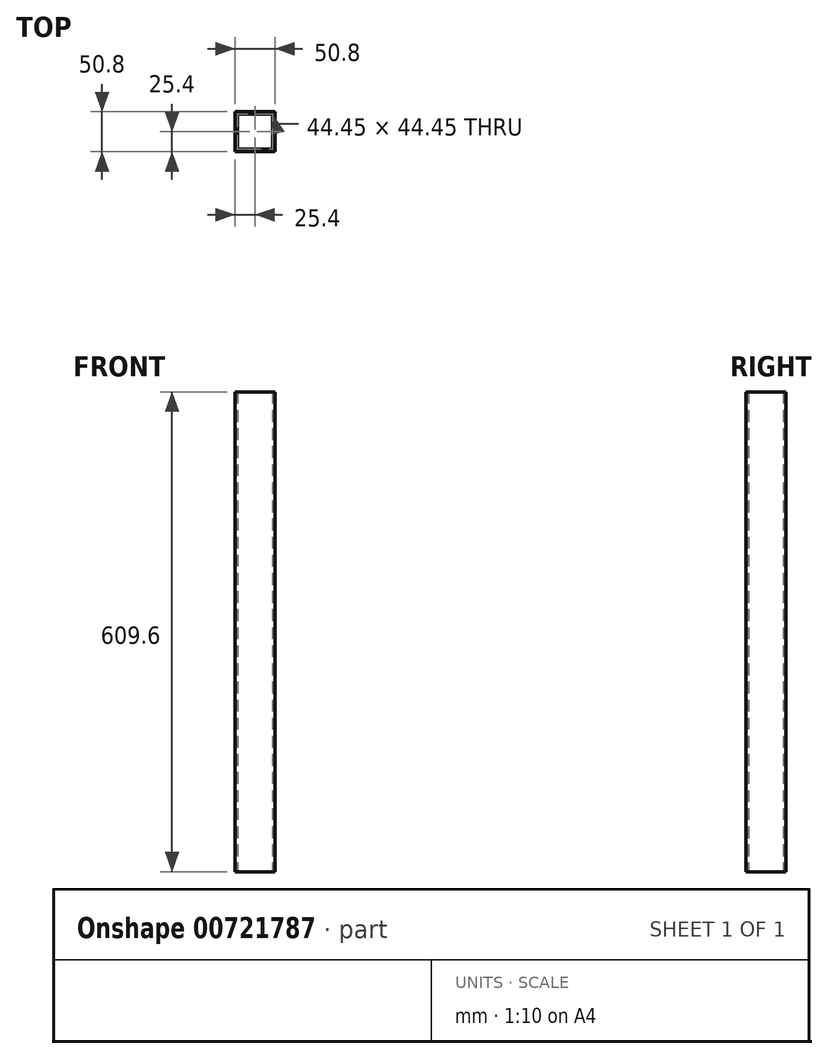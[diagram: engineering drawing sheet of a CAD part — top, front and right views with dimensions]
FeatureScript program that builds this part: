
annotation { "Feature Type Name" : "Feature", "Feature Type Description" : "" }
export const myFeature = defineFeature(function(context is Context, id is Id, definition is map)
    precondition{}
    {
        {
            var Q0;
            Q0=qCreatedBy(makeId("Top.planeOp"),FACE);
            var sketch = newSketch(context, id + "F0", { "sketchPlane" : qUnion([Q0])});
            skLineSegment(sketch, "E0.bottom", {"start": v(25.4, 25.4) * mm, "end": v(-25.4, 25.4) * mm});
            skLineSegment(sketch, "E0.top", {"start": v(25.4, -25.4) * mm, "end": v(-25.4, -25.4) * mm});
            skLineSegment(sketch, "E0.left", {"start": v(25.4, 25.4) * mm, "end": v(25.4, -25.4) * mm});
            skLineSegment(sketch, "E0.right", {"start": v(-25.4, 25.4) * mm, "end": v(-25.4, -25.4) * mm});
            skPoint(sketch, "E0.middle", {"position": v(0, 0) * mm});
            skLineSegment(sketch, "E1.0", {"start": v(22.23, 22.23) * mm, "end": v(-22.22, 22.23) * mm});
            skLineSegment(sketch, "E1.1", {"start": v(22.23, 22.23) * mm, "end": v(22.23, -22.22) * mm});
            skLineSegment(sketch, "E1.2", {"start": v(22.23, -22.22) * mm, "end": v(-22.22, -22.22) * mm});
            skLineSegment(sketch, "E1.3", {"start": v(-22.22, 22.23) * mm, "end": v(-22.22, -22.22) * mm});
            skSolve(sketch);
        }
        {
            var Q0;
            Q0=makeQuery(id+"F0.imprint","IMPRINT",FACE,{"disambiguationData":[TD([[makeQuery(id+"F0.imprint","IMPRINT",EDGE,{"derivedFrom":sQuery(id+"F0.wireOp",EDGE,"E0.bottom")}),1.0]])]});
            extrude(context, id + "F1", {"entities" : qUnion([Q0]), "depth" : 609.6 * mm, "offsetDistance" : 25.4 * mm});
        }
    });
